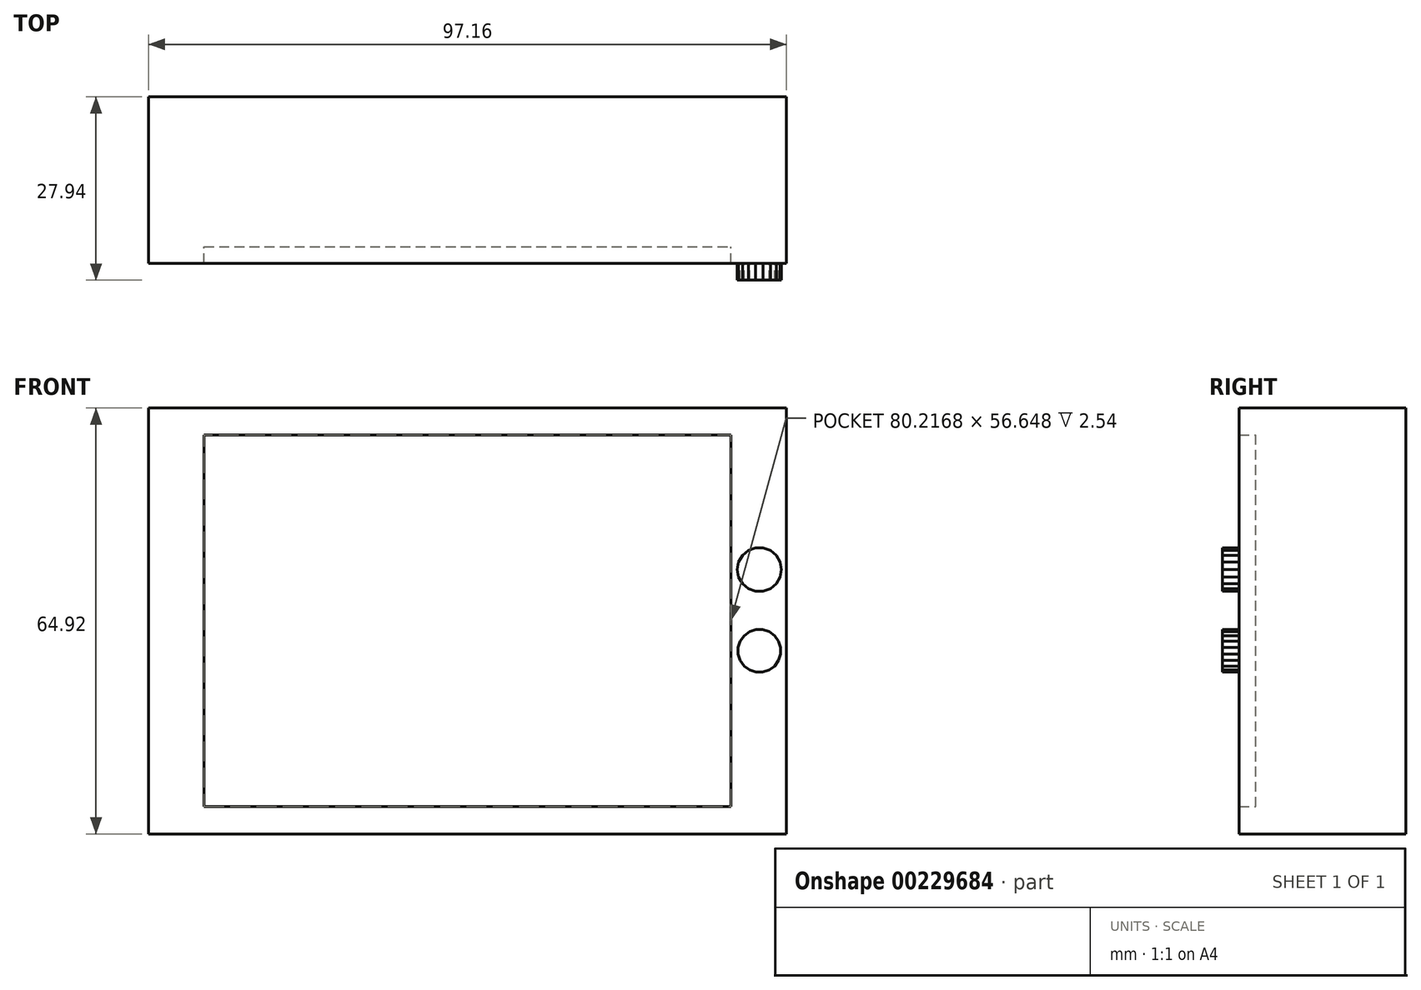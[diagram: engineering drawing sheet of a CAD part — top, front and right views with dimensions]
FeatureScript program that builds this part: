
annotation { "Feature Type Name" : "Feature", "Feature Type Description" : "" }
export const myFeature = defineFeature(function(context is Context, id is Id, definition is map)
    precondition{}
    {
        {
            var Q0;
            Q0=qCreatedBy(makeId("Front.planeOp"),FACE);
            var sketch = newSketch(context, id + "F0", { "sketchPlane" : qUnion([Q0])});
            skLineSegment(sketch, "E0.bottom", {"start": v(-48.58, -32.46) * mm, "end": v(48.58, -32.46) * mm});
            skLineSegment(sketch, "E0.top", {"start": v(-48.58, 32.46) * mm, "end": v(48.58, 32.46) * mm});
            skLineSegment(sketch, "E0.left", {"start": v(-48.58, -32.46) * mm, "end": v(-48.58, 32.46) * mm});
            skLineSegment(sketch, "E0.right", {"start": v(48.58, -32.46) * mm, "end": v(48.58, 32.46) * mm});
            skPoint(sketch, "E0.middle", {"position": v(0, 0) * mm});
            skLineSegment(sketch, "E1.bottom", {"start": v(-40.1, -28.32) * mm, "end": v(40.1, -28.32) * mm});
            skLineSegment(sketch, "E1.top", {"start": v(-40.1, 28.32) * mm, "end": v(40.1, 28.32) * mm});
            skLineSegment(sketch, "E1.left", {"start": v(-40.1, -28.32) * mm, "end": v(-40.1, 28.32) * mm});
            skLineSegment(sketch, "E1.right", {"start": v(40.1, -28.32) * mm, "end": v(40.1, 28.32) * mm});
            skLineSegment(sketch, "E2", {"start": v(23.21, 32.46) * mm, "end": v(16.8, 43.47) * mm});
            skLineSegment(sketch, "E3", {"start": v(23.21, 32.46) * mm, "end": v(31.7, 42.45) * mm});
            skArc(sketch, "E4.cCircle", {"start": v(43.32, 10.96) * mm, "mid": v(41.14, 7.86) * mm, "end": v(43.32, 4.75) * mm, "construction": true});
            skLineSegment(sketch, "E4.0", {"start": v(45.03, 4.55) * mm, "end": v(43.87, 4.55) * mm});
            skLineSegment(sketch, "E4.1", {"start": v(43.87, 4.55) * mm, "end": v(42.77, 4.95) * mm});
            skLineSegment(sketch, "E4.2", {"start": v(42.77, 4.95) * mm, "end": v(41.88, 5.7) * mm});
            skLineSegment(sketch, "E4.3", {"start": v(41.88, 5.7) * mm, "end": v(41.3, 6.7) * mm});
            skLineSegment(sketch, "E4.4", {"start": v(41.3, 6.7) * mm, "end": v(41.1, 7.86) * mm});
            skLineSegment(sketch, "E4.5", {"start": v(41.1, 7.86) * mm, "end": v(41.3, 9) * mm});
            skLineSegment(sketch, "E4.6", {"start": v(41.3, 9) * mm, "end": v(41.88, 10.02) * mm});
            skLineSegment(sketch, "E4.7", {"start": v(41.88, 10.02) * mm, "end": v(42.77, 10.77) * mm});
            skLineSegment(sketch, "E4.8", {"start": v(42.77, 10.77) * mm, "end": v(43.87, 11.16) * mm});
            skLineSegment(sketch, "E4.9", {"start": v(43.87, 11.16) * mm, "end": v(45.03, 11.16) * mm});
            skLineSegment(sketch, "E4.10", {"start": v(45.03, 11.16) * mm, "end": v(46.13, 10.77) * mm});
            skLineSegment(sketch, "E4.11", {"start": v(46.13, 10.77) * mm, "end": v(47.02, 10.02) * mm});
            skLineSegment(sketch, "E4.12", {"start": v(47.02, 10.02) * mm, "end": v(47.6, 9) * mm});
            skLineSegment(sketch, "E4.13", {"start": v(47.6, 9) * mm, "end": v(47.8, 7.86) * mm});
            skLineSegment(sketch, "E4.14", {"start": v(47.8, 7.86) * mm, "end": v(47.6, 6.7) * mm});
            skLineSegment(sketch, "E4.15", {"start": v(47.6, 6.7) * mm, "end": v(47.02, 5.7) * mm});
            skLineSegment(sketch, "E4.16", {"start": v(47.02, 5.7) * mm, "end": v(46.13, 4.95) * mm});
            skLineSegment(sketch, "E4.17", {"start": v(46.13, 4.95) * mm, "end": v(45.03, 4.55) * mm});
            skPoint(sketch, "E4.0.midPoint", {"position": v(44.45, 4.55) * mm});
            skArc(sketch, "E5.cCircle", {"start": v(42.55, -1.93) * mm, "mid": v(41.37, -5.55) * mm, "end": v(44.45, -7.79) * mm, "construction": true});
            skLineSegment(sketch, "E5.0", {"start": v(44.96, -7.79) * mm, "end": v(43.94, -7.79) * mm});
            skLineSegment(sketch, "E5.1", {"start": v(43.94, -7.79) * mm, "end": v(42.96, -7.47) * mm});
            skLineSegment(sketch, "E5.2", {"start": v(42.96, -7.47) * mm, "end": v(42.13, -6.87) * mm});
            skLineSegment(sketch, "E5.3", {"start": v(42.13, -6.87) * mm, "end": v(41.53, -6.04) * mm});
            skLineSegment(sketch, "E5.4", {"start": v(41.53, -6.04) * mm, "end": v(41.21, -5.06) * mm});
            skLineSegment(sketch, "E5.5", {"start": v(41.21, -5.06) * mm, "end": v(41.21, -4.04) * mm});
            skLineSegment(sketch, "E5.6", {"start": v(41.21, -4.04) * mm, "end": v(41.53, -3.06) * mm});
            skLineSegment(sketch, "E5.7", {"start": v(41.53, -3.06) * mm, "end": v(42.13, -2.23) * mm});
            skLineSegment(sketch, "E5.8", {"start": v(42.13, -2.23) * mm, "end": v(42.96, -1.63) * mm});
            skLineSegment(sketch, "E5.9", {"start": v(42.96, -1.63) * mm, "end": v(43.94, -1.31) * mm});
            skLineSegment(sketch, "E5.10", {"start": v(43.94, -1.31) * mm, "end": v(44.96, -1.31) * mm});
            skLineSegment(sketch, "E5.11", {"start": v(44.96, -1.31) * mm, "end": v(45.94, -1.63) * mm});
            skLineSegment(sketch, "E5.12", {"start": v(45.94, -1.63) * mm, "end": v(46.77, -2.23) * mm});
            skLineSegment(sketch, "E5.13", {"start": v(46.77, -2.23) * mm, "end": v(47.37, -3.06) * mm});
            skLineSegment(sketch, "E5.14", {"start": v(47.37, -3.06) * mm, "end": v(47.69, -4.04) * mm});
            skLineSegment(sketch, "E5.15", {"start": v(47.69, -4.04) * mm, "end": v(47.69, -5.06) * mm});
            skLineSegment(sketch, "E5.16", {"start": v(47.69, -5.06) * mm, "end": v(47.37, -6.04) * mm});
            skLineSegment(sketch, "E5.17", {"start": v(47.37, -6.04) * mm, "end": v(46.77, -6.87) * mm});
            skLineSegment(sketch, "E5.18", {"start": v(46.77, -6.87) * mm, "end": v(45.94, -7.47) * mm});
            skLineSegment(sketch, "E5.19", {"start": v(45.94, -7.47) * mm, "end": v(44.96, -7.79) * mm});
            skPoint(sketch, "E5.0.midPoint", {"position": v(44.45, -7.79) * mm});
            skArc(sketch, "E6.trimOffspring", {"start": v(45.58, 4.75) * mm, "mid": v(46.1, 5) * mm, "end": v(46.58, 5.32) * mm, "construction": true});
            skArc(sketch, "E7.trimOffspring", {"start": v(47.31, 6.2) * mm, "mid": v(47.7, 8.43) * mm, "end": v(46.58, 10.4) * mm, "construction": true});
            skArc(sketch, "E8.trimOffspring", {"start": v(45.58, 10.96) * mm, "mid": v(45.02, 11.11) * mm, "end": v(44.45, 11.16) * mm, "construction": true});
            skArc(sketch, "E9.trimOffspring", {"start": v(45.45, -7.63) * mm, "mid": v(47.53, -3.55) * mm, "end": v(43.45, -1.47) * mm, "construction": true});
            skSolve(sketch);
        }
        {
            var Q0;
            Q0=makeQuery(id+"F0.imprint","IMPRINT",FACE,{"disambiguationData":[TD([[makeQuery(id+"F0.imprint","IMPRINT",EDGE,{"derivedFrom":sQuery(id+"F0.wireOp",EDGE,"E0.bottom")}),1.0]])]});
            extrude(context, id + "F1", {"entities" : qUnion([Q0]), "depth" : 25.4 * mm});
        }
        {
            var Q0;
            Q0=makeQuery(id+"F0.imprint","IMPRINT",FACE,{"disambiguationData":[TD([[makeQuery(id+"F0.imprint","IMPRINT",EDGE,{"derivedFrom":sQuery(id+"F0.wireOp",EDGE,"E1.bottom")}),1.0]])]});
            extrude(context, id + "F2", {"entities" : qUnion([Q0]), "operationType" : NewBodyOperationType.ADD, "depth" : 22.86 * mm});
        }
        {
            var Q0;
            Q0=makeQuery(id+"F0.imprint","IMPRINT",FACE,{"disambiguationData":[TD([[makeQuery(id+"F0.imprint","IMPRINT",EDGE,{"derivedFrom":sQuery(id+"F0.wireOp",EDGE,"E4.0")}),-1.0]])]});
            extrude(context, id + "F3", {"entities" : qUnion([Q0]), "operationType" : NewBodyOperationType.ADD, "depth" : 27.94 * mm});
        }
        {
            var Q0;
            Q0=makeQuery(id+"F0.imprint","IMPRINT",FACE,{"disambiguationData":[TD([[makeQuery(id+"F0.imprint","IMPRINT",EDGE,{"derivedFrom":sQuery(id+"F0.wireOp",EDGE,"E5.0")}),-1.0]])]});
            extrude(context, id + "F4", {"entities" : qUnion([Q0]), "operationType" : NewBodyOperationType.ADD, "depth" : 27.94 * mm});
        }
        {
            var Q0;
            Q0=sQuery(id+"F0.wireOp",EDGE,"E2");
            extrude(context, id + "F5", {"bodyType" : ToolBodyType.SURFACE, "surfaceEntities" : qUnion([Q0]), "depth" : 0.25 * mm});
        }
        {
            var Q0;
            Q0=sQuery(id+"F0.wireOp",EDGE,"E3");
            extrude(context, id + "F6", {"bodyType" : ToolBodyType.SURFACE, "surfaceEntities" : qUnion([Q0]), "depth" : 0.25 * mm});
        }
    });
